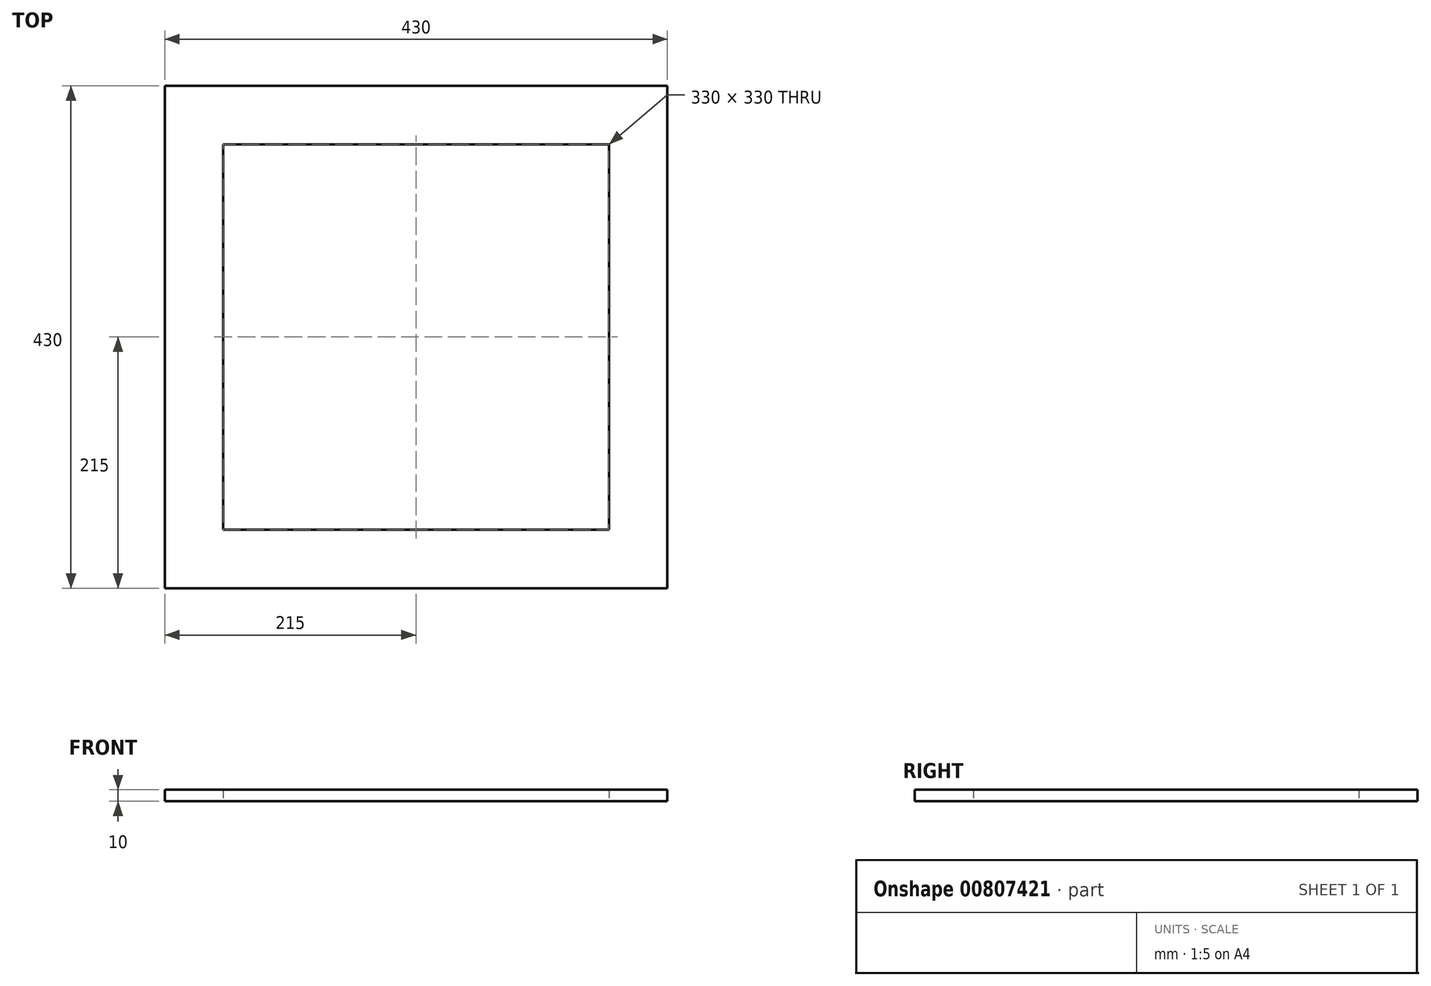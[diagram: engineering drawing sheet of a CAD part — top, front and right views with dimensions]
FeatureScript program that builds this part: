
annotation { "Feature Type Name" : "Feature", "Feature Type Description" : "" }
export const myFeature = defineFeature(function(context is Context, id is Id, definition is map)
    precondition{}
    {
        {
            var Q0;
            Q0=qCreatedBy(makeId("Top.planeOp"),FACE);
            var sketch = newSketch(context, id + "F0", { "sketchPlane" : qUnion([Q0])});
            skLineSegment(sketch, "E0.bottom", {"start": v(215, -215) * mm, "end": v(-215, -215) * mm});
            skLineSegment(sketch, "E0.top", {"start": v(215, 215) * mm, "end": v(-215, 215) * mm});
            skLineSegment(sketch, "E0.left", {"start": v(215, -215) * mm, "end": v(215, 215) * mm});
            skLineSegment(sketch, "E0.right", {"start": v(-215, -215) * mm, "end": v(-215, 215) * mm});
            skPoint(sketch, "E0.middle", {"position": v(0, 0) * mm});
            skLineSegment(sketch, "E1.bottom", {"start": v(165, -165) * mm, "end": v(-165, -165) * mm});
            skLineSegment(sketch, "E1.top", {"start": v(165, 165) * mm, "end": v(-165, 165) * mm});
            skLineSegment(sketch, "E1.left", {"start": v(165, -165) * mm, "end": v(165, 165) * mm});
            skLineSegment(sketch, "E1.right", {"start": v(-165, -165) * mm, "end": v(-165, 165) * mm});
            skSolve(sketch);
        }
        {
            var Q0;
            Q0=makeQuery(id+"F0.imprint","IMPRINT",FACE,{"disambiguationData":[TD([[makeQuery(id+"F0.imprint","IMPRINT",EDGE,{"derivedFrom":sQuery(id+"F0.wireOp",EDGE,"E0.bottom")}),-1.0]])]});
            extrude(context, id + "F1", {"entities" : qUnion([Q0]), "depth" : 10 * mm, "offsetDistance" : 25 * mm});
        }
    });
